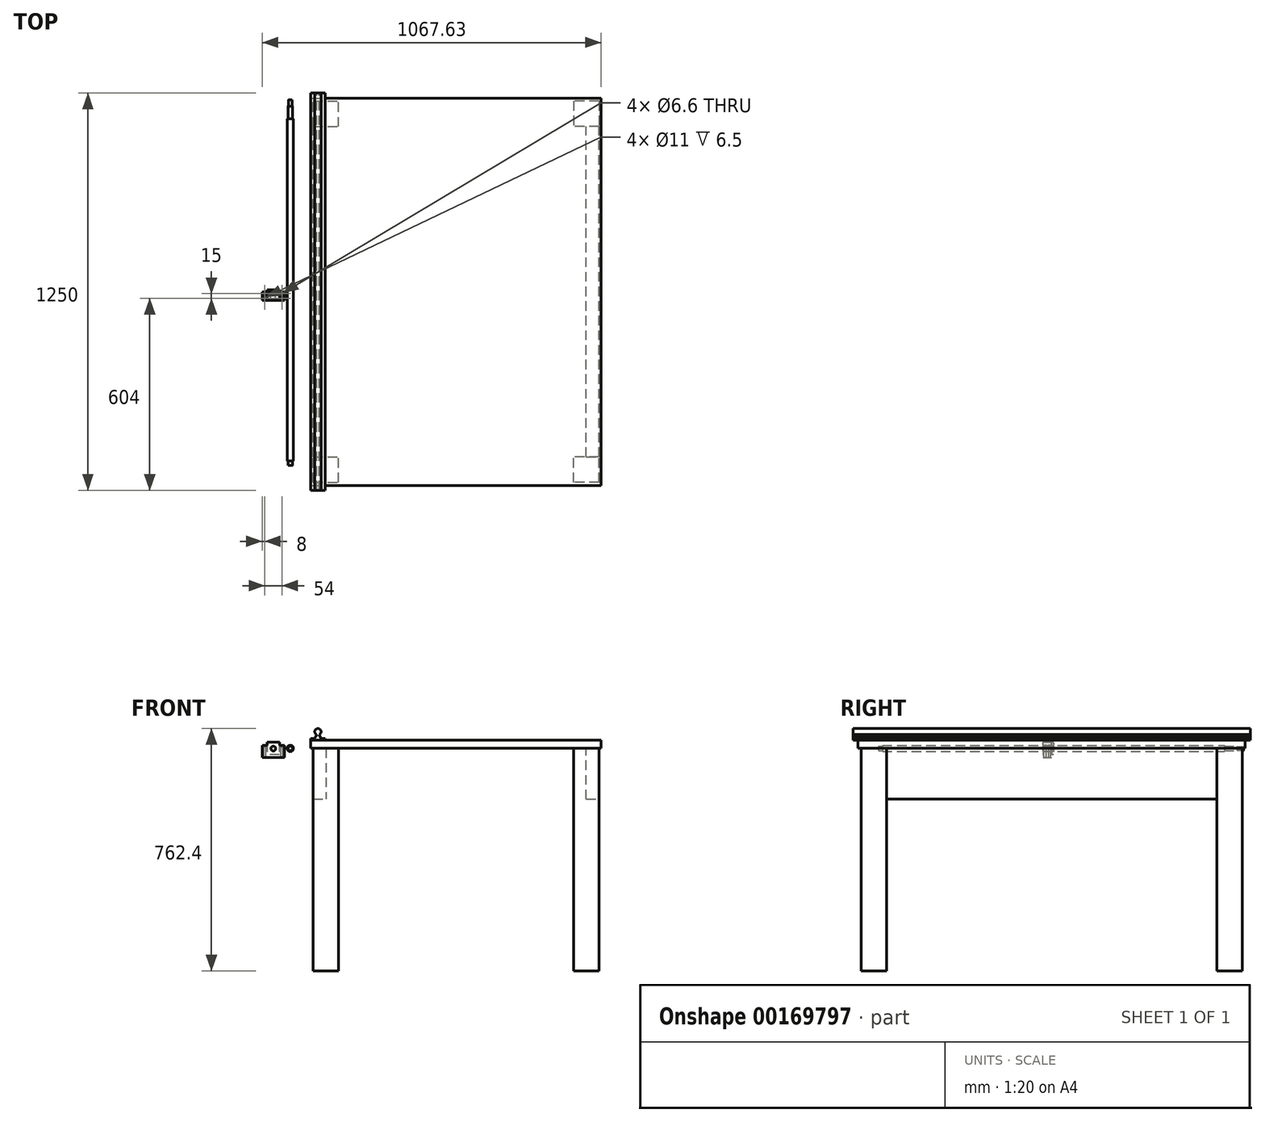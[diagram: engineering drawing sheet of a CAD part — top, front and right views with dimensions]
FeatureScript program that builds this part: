
annotation { "Feature Type Name" : "Feature", "Feature Type Description" : "" }
export const myFeature = defineFeature(function(context is Context, id is Id, definition is map)
    precondition{}
    {
        {
            var Q0;
            Q0=qCreatedBy(makeId("Top.planeOp"),FACE);
            var sketch = newSketch(context, id + "F0", { "sketchPlane" : qUnion([Q0])});
            skLineSegment(sketch, "E0.bottom", {"start": v(-410, -560) * mm, "end": v(410, -560) * mm, "construction": true});
            skLineSegment(sketch, "E0.top", {"start": v(-410, 560) * mm, "end": v(410, 560) * mm, "construction": true});
            skLineSegment(sketch, "E0.left", {"start": v(-410, -560) * mm, "end": v(-410, 560) * mm, "construction": true});
            skLineSegment(sketch, "E0.right", {"start": v(410, -560) * mm, "end": v(410, 560) * mm, "construction": true});
            skPoint(sketch, "E0.middle", {"position": v(0, 0) * mm});
            skLineSegment(sketch, "E1.bottom", {"start": v(-450, 520) * mm, "end": v(-370, 520) * mm});
            skLineSegment(sketch, "E1.top", {"start": v(-450, 600) * mm, "end": v(-370, 600) * mm});
            skLineSegment(sketch, "E1.left", {"start": v(-450, 520) * mm, "end": v(-450, 600) * mm});
            skLineSegment(sketch, "E1.right", {"start": v(-370, 520) * mm, "end": v(-370, 600) * mm});
            skPoint(sketch, "E1.middle", {"position": v(-410, 560) * mm});
            skLineSegment(sketch, "E2.bottom", {"start": v(-450, -600) * mm, "end": v(-370, -600) * mm});
            skLineSegment(sketch, "E2.top", {"start": v(-450, -520) * mm, "end": v(-370, -520) * mm});
            skLineSegment(sketch, "E2.left", {"start": v(-450, -600) * mm, "end": v(-450, -520) * mm});
            skLineSegment(sketch, "E2.right", {"start": v(-370, -600) * mm, "end": v(-370, -520) * mm});
            skPoint(sketch, "E2.middle", {"position": v(-410, -560) * mm});
            skLineSegment(sketch, "E3.bottom", {"start": v(450, 600) * mm, "end": v(370, 600) * mm});
            skLineSegment(sketch, "E3.top", {"start": v(450, 520) * mm, "end": v(370, 520) * mm});
            skLineSegment(sketch, "E3.left", {"start": v(450, 600) * mm, "end": v(450, 520) * mm});
            skLineSegment(sketch, "E3.right", {"start": v(370, 600) * mm, "end": v(370, 520) * mm});
            skPoint(sketch, "E3.middle", {"position": v(410, 560) * mm});
            skLineSegment(sketch, "E4.bottom", {"start": v(450, -600) * mm, "end": v(370, -600) * mm});
            skLineSegment(sketch, "E4.top", {"start": v(450, -520) * mm, "end": v(370, -520) * mm});
            skLineSegment(sketch, "E4.left", {"start": v(450, -600) * mm, "end": v(450, -520) * mm});
            skLineSegment(sketch, "E4.right", {"start": v(370, -600) * mm, "end": v(370, -520) * mm});
            skPoint(sketch, "E4.middle", {"position": v(410, -560) * mm});
            skLineSegment(sketch, "E5.bottom", {"start": v(-457.2, -609.6) * mm, "end": v(457.2, -609.6) * mm});
            skLineSegment(sketch, "E5.top", {"start": v(-457.2, 609.6) * mm, "end": v(457.2, 609.6) * mm});
            skLineSegment(sketch, "E5.left", {"start": v(-457.2, -609.6) * mm, "end": v(-457.2, 609.6) * mm});
            skLineSegment(sketch, "E5.right", {"start": v(457.2, -609.6) * mm, "end": v(457.2, 609.6) * mm});
            skSolve(sketch);
        }
        {
            var Q0;
            Q0=makeQuery(id+"F0.imprint","IMPRINT",FACE,{"disambiguationData":[TD([[makeQuery(id+"F0.imprint","IMPRINT",EDGE,{"derivedFrom":sQuery(id+"F0.wireOp",EDGE,"E1.bottom")}),1.0]])]});
            var Q1;
            Q1=makeQuery(id+"F0.imprint","IMPRINT",FACE,{"disambiguationData":[TD([[makeQuery(id+"F0.imprint","IMPRINT",EDGE,{"derivedFrom":sQuery(id+"F0.wireOp",EDGE,"E3.bottom")}),1.0]])]});
            var Q2;
            Q2=makeQuery(id+"F0.imprint","IMPRINT",FACE,{"disambiguationData":[TD([[makeQuery(id+"F0.imprint","IMPRINT",EDGE,{"derivedFrom":sQuery(id+"F0.wireOp",EDGE,"E4.bottom")}),-1.0]])]});
            var Q3;
            Q3=makeQuery(id+"F0.imprint","IMPRINT",FACE,{"disambiguationData":[TD([[makeQuery(id+"F0.imprint","IMPRINT",EDGE,{"derivedFrom":sQuery(id+"F0.wireOp",EDGE,"E2.bottom")}),1.0]])]});
            extrude(context, id + "F1", {"entities" : qUnion([Q0, Q1, Q2, Q3]), "oppositeDirection" : true, "depth" : 700 * mm});
        }
        {
            var Q0;
            Q0=makeQuery(id+"F1.opExtrude","SWEPT_FACE",FACE,{"disambiguationData":[OSD([sQuery(id+"F0.wireOp",EDGE,"E1.bottom")])]});
            var sketch = newSketch(context, id + "F2", { "sketchPlane" : qUnion([Q0])});
            skLineSegment(sketch, "E6.bottom", {"start": v(-450, 0) * mm, "end": v(-410, 0) * mm});
            skLineSegment(sketch, "E6.top", {"start": v(-450, -160) * mm, "end": v(-410, -160) * mm});
            skLineSegment(sketch, "E6.left", {"start": v(-450, 0) * mm, "end": v(-450, -160) * mm});
            skLineSegment(sketch, "E6.right", {"start": v(-410, 0) * mm, "end": v(-410, -160) * mm});
            skLineSegment(sketch, "E7.bottom", {"start": v(450, 0) * mm, "end": v(410, 0) * mm});
            skLineSegment(sketch, "E7.top", {"start": v(450, -160) * mm, "end": v(410, -160) * mm});
            skLineSegment(sketch, "E7.left", {"start": v(450, 0) * mm, "end": v(450, -160) * mm});
            skLineSegment(sketch, "E7.right", {"start": v(410, 0) * mm, "end": v(410, -160) * mm});
            skSolve(sketch);
        }
        {
            var Q0;
            Q0 = qSketchRegion(id + "F2", true);
            extrude(context, id + "F3", {"entities" : qUnion([Q0]), "endBound" : BoundingType.UP_TO_NEXT, "depth" : 25 * mm});
        }
        {
            var Q0;
            Q0=makeQuery(id+"F0.imprint","IMPRINT",FACE,{"disambiguationData":[TD([[makeQuery(id+"F0.imprint","IMPRINT",EDGE,{"derivedFrom":sQuery(id+"F0.wireOp",EDGE,"E1.bottom")}),1.0]])]});
            var Q1;
            Q1=makeQuery(id+"F0.imprint","IMPRINT",FACE,{"disambiguationData":[TD([[makeQuery(id+"F0.imprint","IMPRINT",EDGE,{"derivedFrom":sQuery(id+"F0.wireOp",EDGE,"E1.bottom")}),-1.0]])]});
            var Q2;
            Q2=makeQuery(id+"F0.imprint","IMPRINT",FACE,{"disambiguationData":[TD([[makeQuery(id+"F0.imprint","IMPRINT",EDGE,{"derivedFrom":sQuery(id+"F0.wireOp",EDGE,"E3.bottom")}),1.0]])]});
            var Q3;
            Q3=makeQuery(id+"F0.imprint","IMPRINT",FACE,{"disambiguationData":[TD([[makeQuery(id+"F0.imprint","IMPRINT",EDGE,{"derivedFrom":sQuery(id+"F0.wireOp",EDGE,"E4.bottom")}),-1.0]])]});
            var Q4;
            Q4=makeQuery(id+"F0.imprint","IMPRINT",FACE,{"disambiguationData":[TD([[makeQuery(id+"F0.imprint","IMPRINT",EDGE,{"derivedFrom":sQuery(id+"F0.wireOp",EDGE,"E2.bottom")}),1.0]])]});
            extrude(context, id + "F4", {"entities" : qUnion([Q0, Q1, Q2, Q3, Q4]), "depth" : 25.4 * mm});
        }
        {
            var Q0;
            Q0=qCreatedBy(makeId("Front.planeOp"),FACE);
            var sketch = newSketch(context, id + "F5", { "sketchPlane" : qUnion([Q0])});
            skLineSegment(sketch, "E8.bottom", {"start": v(-457.5, 25.4) * mm, "end": v(-412.5, 25.4) * mm});
            skLineSegment(sketch, "E9", {"start": v(0, 0) * mm, "end": v(0, 53.76) * mm, "construction": true});
            skLineSegment(sketch, "E10", {"start": v(-457.5, 25.4) * mm, "end": v(-457.5, 30.4) * mm});
            skLineSegment(sketch, "E11", {"start": v(-444.5, 35.4) * mm, "end": v(-442.93, 35.4) * mm});
            skLineSegment(sketch, "E12", {"start": v(-442.93, 35.4) * mm, "end": v(-439.23, 43.34) * mm});
            skLineSegment(sketch, "E13", {"start": v(-430.77, 43.34) * mm, "end": v(-427.07, 35.4) * mm});
            skLineSegment(sketch, "E14", {"start": v(-427.07, 35.4) * mm, "end": v(-425.5, 35.4) * mm});
            skLineSegment(sketch, "E15", {"start": v(-412.5, 30.4) * mm, "end": v(-412.5, 25.4) * mm});
            skArc(sketch, "E16", {"start": v(-430.77, 43.34) * mm, "mid": v(-435, 62.4) * mm, "end": v(-439.23, 43.34) * mm});
            skLineSegment(sketch, "E17", {"start": v(-435, 52.4) * mm, "end": v(-435, 25.4) * mm, "construction": true});
            skLineSegment(sketch, "E18", {"start": v(-444.5, 35.4) * mm, "end": v(-444.5, 30.4) * mm});
            skLineSegment(sketch, "E19", {"start": v(-444.5, 30.4) * mm, "end": v(-457.5, 30.4) * mm});
            skLineSegment(sketch, "E20", {"start": v(-425.5, 35.4) * mm, "end": v(-425.5, 30.4) * mm});
            skLineSegment(sketch, "E21", {"start": v(-425.5, 30.4) * mm, "end": v(-412.5, 30.4) * mm});
            skSolve(sketch);
        }
        {
            var Q0;
            Q0 = qSketchRegion(id + "F5", true);
            var Q1;
            Q1=makeQuery(id+"F4.opExtrude","SWEPT_FACE",FACE,{"disambiguationData":[OSD([sQuery(id+"F0.wireOp",EDGE,"E5.bottom")])]});
            extrude(context, id + "F6", {"entities" : qUnion([Q0]), "endBound" : BoundingType.SYMMETRIC, "depth" : 1250 * mm, "endBoundEntityFace" : qUnion([Q1]), "offsetDistance" : 25 * mm});
        }
        {
            var Q0;
            Q0=qCreatedBy(makeId("Top.planeOp"),FACE);
            var sketch = newSketch(context, id + "F7", { "sketchPlane" : qUnion([Q0])});
            skLineSegment(sketch, "E22", {"start": v(-521.9, 636.45) * mm, "end": v(-521.9, 604.04) * mm, "construction": true});
            skLineSegment(sketch, "E23", {"start": v(-521.9, 604.04) * mm, "end": v(-515.9, 604.04) * mm});
            skLineSegment(sketch, "E24", {"start": v(-515.9, 604.04) * mm, "end": v(-515.9, 584.04) * mm});
            skLineSegment(sketch, "E25", {"start": v(-515.9, 584.04) * mm, "end": v(-514.4, 584.04) * mm});
            skLineSegment(sketch, "E26", {"start": v(-514.4, 584.04) * mm, "end": v(-514.4, 544.04) * mm});
            skLineSegment(sketch, "E27", {"start": v(-514.4, 544.04) * mm, "end": v(-511.9, 544.04) * mm});
            skLineSegment(sketch, "E28", {"start": v(-511.9, 544.04) * mm, "end": v(-511.9, -532.96) * mm});
            skLineSegment(sketch, "E29", {"start": v(-511.9, -532.96) * mm, "end": v(-514.4, -532.96) * mm});
            skLineSegment(sketch, "E30", {"start": v(-514.4, -532.96) * mm, "end": v(-514.4, -545.96) * mm});
            skLineSegment(sketch, "E31", {"start": v(-514.4, -545.96) * mm, "end": v(-521.9, -545.96) * mm});
            skLineSegment(sketch, "E32", {"start": v(-521.9, -545.96) * mm, "end": v(-521.9, 604.04) * mm});
            skSolve(sketch);
        }
        {
            var Q0;
            Q0=makeQuery(id+"F7.imprint","IMPRINT",FACE,{"disambiguationData":[TD([[makeQuery(id+"F7.imprint","IMPRINT",EDGE,{"derivedFrom":sQuery(id+"F7.wireOp",EDGE,"E23")}),-1.0]])]});
            var Q1;
            Q1=sQuery(id+"F7.wireOp",EDGE,"E22");
            revolve(context, id + "F8", {"entities" : qUnion([Q0]), "axis" : qUnion([Q1]), "revolveType" : RevolveType.FULL});
        }
        {
            var Q0;
            Q0=qCreatedBy(makeId("Front.planeOp"),FACE);
            var sketch = newSketch(context, id + "F9", { "sketchPlane" : qUnion([Q0])});
            skLineSegment(sketch, "E33.bottom", {"start": v(-540.43, 9.5) * mm, "end": v(-555.43, 9.5) * mm});
            skLineSegment(sketch, "E33.top", {"start": v(-540.43, -28.5) * mm, "end": v(-610.43, -28.5) * mm});
            skLineSegment(sketch, "E33.left", {"start": v(-540.43, 9.5) * mm, "end": v(-540.43, -28.5) * mm});
            skLineSegment(sketch, "E33.right", {"start": v(-610.43, 9.5) * mm, "end": v(-610.43, -28.5) * mm});
            skLineSegment(sketch, "E34", {"start": v(-555.43, 9.5) * mm, "end": v(-555.43, 19.5) * mm});
            skLineSegment(sketch, "E35", {"start": v(-555.43, 19.5) * mm, "end": v(-595.43, 19.5) * mm});
            skLineSegment(sketch, "E36", {"start": v(-595.43, 19.5) * mm, "end": v(-595.43, 9.5) * mm});
            skLineSegment(sketch, "E37.trimOffspring", {"start": v(-595.43, 9.5) * mm, "end": v(-610.43, 9.5) * mm});
            skCircle(sketch, "E38", {"center": v(-575.43, -0.5) * mm, "radius": 7.5 * mm});
            skPoint(sketch, "E38.centerSnap0", {"position": v(-575.43, -28.5) * mm});
            skSolve(sketch);
        }
        {
            var Q0;
            Q0=makeQuery(id+"F9.imprint","IMPRINT",FACE,{"disambiguationData":[TD([[makeQuery(id+"F9.imprint","IMPRINT",EDGE,{"derivedFrom":sQuery(id+"F9.wireOp",EDGE,"E33.bottom")}),1.0]])]});
            extrude(context, id + "F10", {"entities" : qUnion([Q0]), "depth" : 27 * mm, "offsetDistance" : 25 * mm});
        }
        {
            var Q0;
            Q0=makeQuery(id+"F10.opExtrude","SWEPT_FACE",FACE,{"disambiguationData":[OSD([sQuery(id+"F9.wireOp",EDGE,"E37.trimOffspring")])]});
            var sketch = newSketch(context, id + "F11", { "sketchPlane" : qUnion([Q0])});
            skLineSegment(sketch, "E39.bottom", {"start": v(-602.43, -6) * mm, "end": v(-548.43, -6) * mm, "construction": true});
            skLineSegment(sketch, "E39.top", {"start": v(-602.43, -21) * mm, "end": v(-548.43, -21) * mm, "construction": true});
            skLineSegment(sketch, "E39.left", {"start": v(-602.43, -6) * mm, "end": v(-602.43, -21) * mm, "construction": true});
            skLineSegment(sketch, "E39.right", {"start": v(-548.43, -6) * mm, "end": v(-548.43, -21) * mm, "construction": true});
            skLineSegment(sketch, "E40", {"start": v(-575.43, -21) * mm, "end": v(-575.43, -27) * mm, "construction": true});
            skPoint(sketch, "E40.endSnap0", {"position": v(-575.43, -21) * mm});
            skLineSegment(sketch, "E41", {"start": v(-610.43, -13.5) * mm, "end": v(-602.43, -13.5) * mm, "construction": true});
            skPoint(sketch, "E41.endSnap0", {"position": v(-602.43, -13.5) * mm});
            skSolve(sketch);
        }
        {
            var Q0;
            Q0=sQuery(id+"F11.wireOp",VERTEX,"E39.bottom.start");
            var Q1;
            Q1=sQuery(id+"F11.wireOp",VERTEX,"E39.top.start");
            var Q2;
            Q2=sQuery(id+"F11.wireOp",VERTEX,"E39.bottom.end");
            var Q3;
            Q3=sQuery(id+"F11.wireOp",VERTEX,"E39.right.end");
            var Q4;
            Q4=makeQuery(id+"F10.opExtrude","SWEPT_BODY",BODY,{"disambiguationData":[OSD([sQuery(id+"F9.wireOp",EDGE,"E33.bottom"),sQuery(id+"F9.wireOp",EDGE,"E33.top"),sQuery(id+"F9.wireOp",EDGE,"E33.left"),sQuery(id+"F9.wireOp",EDGE,"E33.right"),sQuery(id+"F9.wireOp",EDGE,"E34"),sQuery(id+"F9.wireOp",EDGE,"E35"),sQuery(id+"F9.wireOp",EDGE,"E36"),sQuery(id+"F9.wireOp",EDGE,"E37.trimOffspring"),sQuery(id+"F9.wireOp",EDGE,"E38")])]});
            hole(context, id + "F12", {"style" : HoleStyle.C_BORE, "endStyle" : HoleEndStyle.THROUGH, "holeDiameter" : 6.6 * mm, "cBoreDiameter" : 11 * mm, "cBoreDepth" : 6.5 * mm, "isTappedThrough" : true, "tappedDepth" : 12 * mm, "tapClearance" : 3, "locations" : qUnion([Q0, Q1, Q2, Q3]), "scope" : qUnion([Q4])});
        }
        {
            var Q0;
            Q0=makeQuery(id+"F10.opExtrude","CAP_FACE",FACE,{"disambiguationData":[OSD([sQuery(id+"F9.wireOp",EDGE,"E33.bottom"),sQuery(id+"F9.wireOp",EDGE,"E33.top"),sQuery(id+"F9.wireOp",EDGE,"E33.left"),sQuery(id+"F9.wireOp",EDGE,"E33.right"),sQuery(id+"F9.wireOp",EDGE,"E34"),sQuery(id+"F9.wireOp",EDGE,"E35"),sQuery(id+"F9.wireOp",EDGE,"E36"),sQuery(id+"F9.wireOp",EDGE,"E37.trimOffspring"),sQuery(id+"F9.wireOp",EDGE,"E38")])],"isStart":true});
            var sketch = newSketch(context, id + "F13", { "sketchPlane" : qUnion([Q0])});
            skLineSegment(sketch, "E42.bottom", {"start": v(556.43, 18.5) * mm, "end": v(594.43, 18.5) * mm});
            skLineSegment(sketch, "E42.top", {"start": v(556.43, -19.5) * mm, "end": v(594.43, -19.5) * mm});
            skLineSegment(sketch, "E42.left", {"start": v(556.43, 18.5) * mm, "end": v(556.43, -19.5) * mm});
            skLineSegment(sketch, "E42.right", {"start": v(594.43, 18.5) * mm, "end": v(594.43, -19.5) * mm});
            skLineSegment(sketch, "E43", {"start": v(556.43, -19.5) * mm, "end": v(594.43, 18.5) * mm, "construction": true});
            skPoint(sketch, "E44", {"position": v(575.43, -0.5) * mm});
            skCircle(sketch, "E45.0", {"center": v(575.43, -0.5) * mm, "radius": 7.5 * mm});
            skSolve(sketch);
        }
        {
            var Q0;
            Q0 = qSketchRegion(id + "F13", true);
            extrude(context, id + "F14", {"entities" : qUnion([Q0]), "operationType" : NewBodyOperationType.ADD, "depth" : 6 * mm, "offsetDistance" : 25 * mm});
        }
    });
